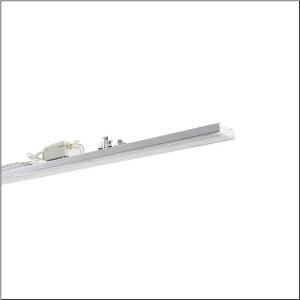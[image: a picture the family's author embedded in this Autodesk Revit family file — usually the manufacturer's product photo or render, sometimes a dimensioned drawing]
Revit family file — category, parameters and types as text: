
# Revit family: licross_11_recessed_mo_51tl10cn49xg
name_source: partatom
category: Lighting Fixtures
units: mm (PartAtom-declared; Revit-internal decimal feet)

## family parameters
Cut with Voids When Loaded = No
Host = Face
Light Source = No
Part Type = Normal
Room Calculation Point = No
Round Connector Dimension = Use Diameter
Shared = No

## types (1)
- --- (1 x LED, 9050 lm, 49.3 W, 4000K)
    Apparent Load = 49 VA
    CIE Flux Codes = 50 81 96 100 100
    Color Rendering = 80
    Color Temperature = 4000K
    Default Elevation = 1800 mm
    Description = Licross 11 Recessed MO, luminaire insert, of sheet steel, coil coated, white, length: 1.500mm, width: 66mm, height: 67mm, LED rated luminous flux: 9.050lm, light colour: 840, SDCM (Standard Deviation of Colour Matching)MacAdam ≤ 2 SDCM (initial), control gear: ON/OFF Multilumen, CLOi, with plug, 3-pole, with phase selection, mains connection: 220..240V, AC, 50/60Hz, start of lifetime: 49W, end of service life: 55W, internal wiring halogen-free, primary optical cover: cover, of PMMA, light emission: direct distribution, primary light characteristic: symmetric, protection rating (complete): IP40, insulation class (complete): insulation class I (protective earthing), certification: CE, ENEC, VDE, UKCA, protection symbol: D if used in an environment without relevant dust loads with corresponding accessories, impact resistance: IK06, permissible ambient temperature for indoor applications: -35..+40°C, corresponds to IFS (International Featured Standards) requirements for safety and quality in the food industry, reducing of maximum allowable ambient temperature of 5°C with ceiling mounting, LABS conformity tested according to VDMA 24364:2018-05, The light source and the operating device comply with the requirements of the Ecodesign Regulation (EU) 2019/2020 and are replaceable in accordance with this regulation, packaging unit: 1 piece
    Height = 58 mm
    Lamp = 1 x LED
    Lamp Light Flux = 9050 lm
    Lamp Power = 49.3 W
    Lamp count = 1
    Length = 1500 mm
    Luminous efficacy = 184 lm/W
    Manufacturer = Siteco
    ModVariant = No
    Model = 51TL10CN49XG
    Mounting Place = Ceiling
    Mounting Type = Pendant
    Number of Poles = 1
    OnlyDefault = Yes
    Power Factor = 1
    Product Name = Licross 11 Recessed MO
    Product group = luminaire insert | ceiling pendant
    ProductGroupID = 901
    Protection Class = Protection class I
    Protection Degree = IP 40
    RLX_Detail_Level = 1
    RLX_Emergency_Light_Flux = 0 lm
    RLX_Emergency_Type = 0
    RLX_Emergency_Type_DB = No
    RlxData = <blob elided: 22421 chars, md5=8ce56205>
    Socket = socket
    Standby Power = 0 W
    System Light Flux = 9050 lm
    System Power = 49 W
    Type Comments = factory setting: luminous flux: 100 % | (A | C | E) | 113 mA
    Type Image = l_1296930.jpg
    URL = http://relux.com
    VarID = @adj_000437
    Voltage = 0 V
    Weight = 0.00 kg
    Width = 66 mm

## geometry (parser evidence)
native form markers: Blend x4, Sweep x10
no freeform markers — native parametric forms only
